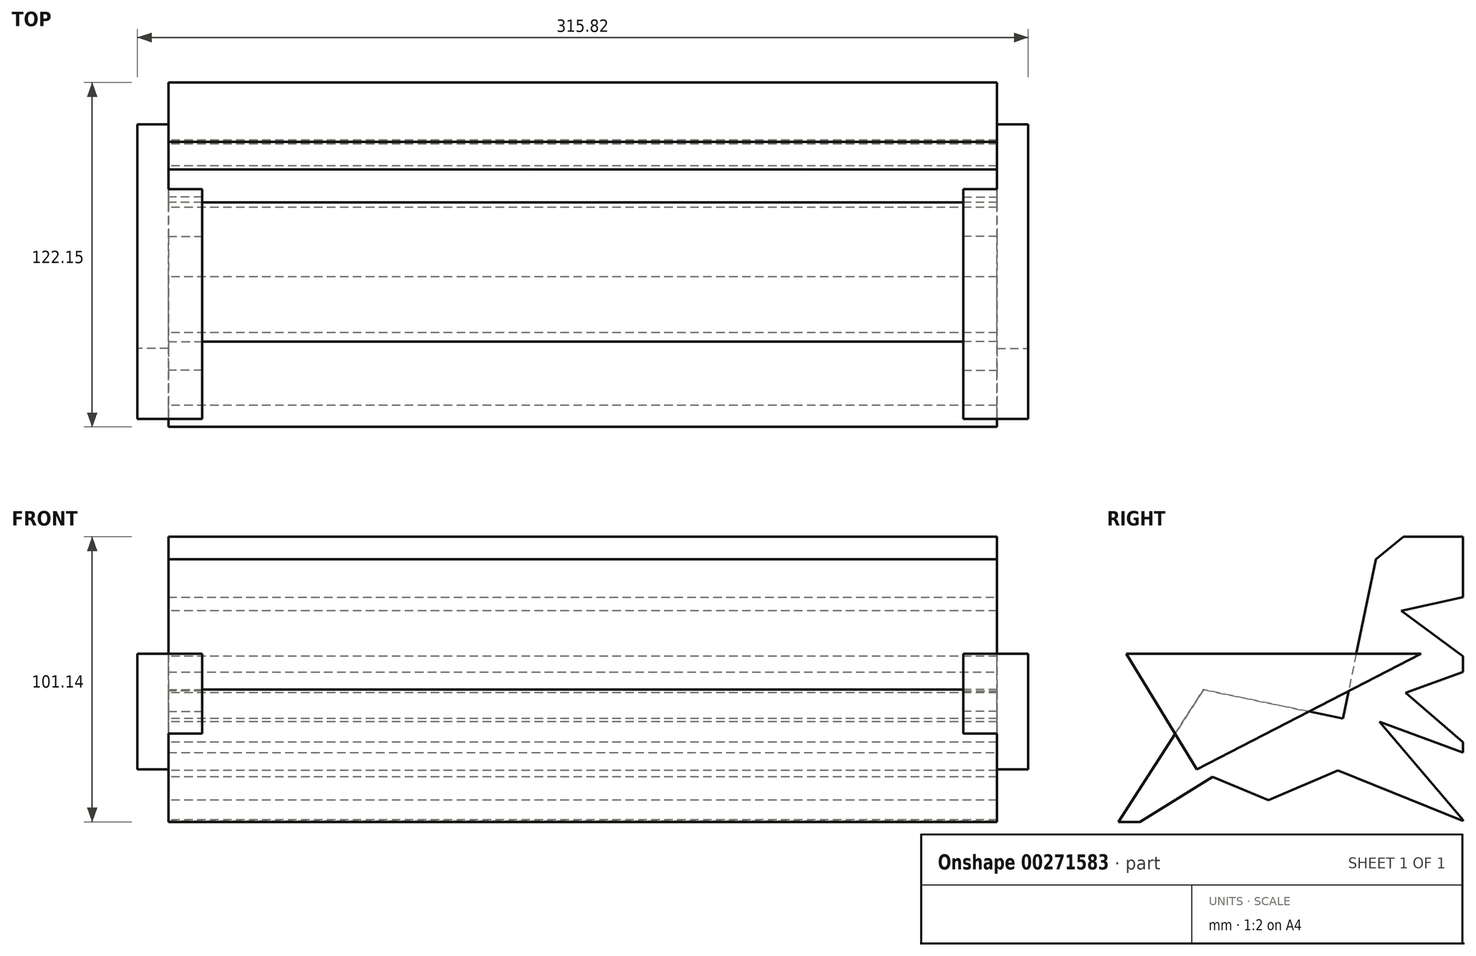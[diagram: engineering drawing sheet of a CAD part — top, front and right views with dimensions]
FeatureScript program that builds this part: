
annotation { "Feature Type Name" : "Feature", "Feature Type Description" : "" }
export const myFeature = defineFeature(function(context is Context, id is Id, definition is map)
    precondition{}
    {
        {
            var Q0;
            Q0=qCreatedBy(makeId("Front.planeOp"),FACE);
            var sketch = newSketch(context, id + "F0", { "sketchPlane" : qUnion([Q0])});
            skLineSegment(sketch, "E0.bottom", {"start": v(-146.91, -50.57) * mm, "end": v(146.91, -50.57) * mm});
            skLineSegment(sketch, "E0.top", {"start": v(-146.91, 50.57) * mm, "end": v(146.91, 50.57) * mm});
            skLineSegment(sketch, "E0.left", {"start": v(-146.91, -50.57) * mm, "end": v(-146.91, 50.57) * mm});
            skLineSegment(sketch, "E0.right", {"start": v(146.91, -50.57) * mm, "end": v(146.91, 50.57) * mm});
            skPoint(sketch, "E0.middle", {"position": v(0, 0) * mm});
            skSolve(sketch);
        }
        {
            var Q0;
            Q0=makeQuery(id+"F0.imprint","IMPRINT",FACE,{"disambiguationData":[TD([[makeQuery(id+"F0.imprint","IMPRINT",EDGE,{"derivedFrom":sQuery(id+"F0.wireOp",EDGE,"E0.bottom")}),1.0]])]});
            extrude(context, id + "F1", {"entities" : qUnion([Q0]), "endBound" : BoundingType.SYMMETRIC, "depth" : 123 * mm});
        }
        {
            var Q0;
            Q0=makeQuery(id+"F1.opExtrude","SWEPT_FACE",FACE,{"disambiguationData":[OSD([sQuery(id+"F0.wireOp",EDGE,"E0.right")])]});
            var sketch = newSketch(context, id + "F2", { "sketchPlane" : qUnion([Q0])});
            skSolve(sketch);
        }
        {
            var Q0;
            {var subQ0=sQuery(id+"F0.wireOp",EDGE,"E0.right");Q0=makeQuery(id+"F2.imprint","IMPRINT",FACE,{"disambiguationData":[TD([[makeQuery(id+"F2.imprint","IMPRINT",EDGE,{"derivedFrom":makeQuery(id+"F1.opExtrude","CAP_EDGE",EDGE,{"disambiguationData":[OSD([subQ0])],"isStart":true})}),1.0]])]});}
            var sketch = newSketch(context, id + "F3", { "sketchPlane" : qUnion([Q0])});
            skLineSegment(sketch, "E1", {"start": v(34.34, 60.4) * mm, "end": v(18.95, -13.91) * mm});
            skLineSegment(sketch, "E2", {"start": v(18.95, -13.91) * mm, "end": v(-30.46, -3.68) * mm});
            skLineSegment(sketch, "E3", {"start": v(-30.46, -3.68) * mm, "end": v(-66.02, -58.91) * mm});
            skLineSegment(sketch, "E4", {"start": v(-66.02, -58.91) * mm, "end": v(-66.02, 65.43) * mm});
            skLineSegment(sketch, "E5", {"start": v(-66.02, 65.43) * mm, "end": v(34.34, 60.4) * mm});
            skSolve(sketch);
        }
        {
            var Q0;
            Q0 = qSketchRegion(id + "F3", true);
            extrude(context, id + "F4", {"entities" : qUnion([Q0]), "operationType" : NewBodyOperationType.REMOVE, "oppositeDirection" : true, "depth" : 334 * mm});
        }
        {
            var Q0;
            {var subQ0=sQuery(id+"F0.wireOp",EDGE,"E0.right");Q0=makeQuery(id+"F2.imprint","IMPRINT",FACE,{"disambiguationData":[TD([[makeQuery(id+"F2.imprint","IMPRINT",EDGE,{"derivedFrom":makeQuery(id+"F1.opExtrude","CAP_EDGE",EDGE,{"disambiguationData":[OSD([subQ0])],"isStart":true})}),1.0]])]});}
            var sketch = newSketch(context, id + "F5", { "sketchPlane" : qUnion([Q0])});
            skLineSegment(sketch, "E6", {"start": v(-32.8, -31.9) * mm, "end": v(-57.89, 9.1) * mm});
            skLineSegment(sketch, "E7", {"start": v(-57.89, 9.1) * mm, "end": v(46.73, 9.1) * mm});
            skLineSegment(sketch, "E8", {"start": v(46.73, 9.1) * mm, "end": v(-32.8, -31.9) * mm});
            skSolve(sketch);
        }
        {
            var Q0;
            Q0=makeQuery(id+"F5.imprint","IMPRINT",FACE,{"disambiguationData":[TD([[makeQuery(id+"F5.imprint","IMPRINT",EDGE,{"derivedFrom":sQuery(id+"F5.wireOp",EDGE,"E6")}),-1.0]])]});
            extrude(context, id + "F6", {"entities" : qUnion([Q0]), "oppositeDirection" : true, "depth" : 12 * mm, "hasSecondDirection" : true, "secondDirectionOppositeDirection" : false, "secondDirectionDepth" : 11 * mm, "offsetDistance" : 25 * mm});
        }
        {
            var Q0;
            Q0=makeQuery(id+"F1.opExtrude","SWEPT_BODY",BODY,{"disambiguationData":[OSD([sQuery(id+"F0.wireOp",EDGE,"E0.bottom"),sQuery(id+"F0.wireOp",EDGE,"E0.top"),sQuery(id+"F0.wireOp",EDGE,"E0.left"),sQuery(id+"F0.wireOp",EDGE,"E0.right")])]});
            var Q1;
            Q1=qCreatedBy(makeId("Right.planeOp"),FACE);
            mirror(context, id + "F7", {"operationType" : NewBodyOperationType.ADD, "entities" : qUnion([Q0]), "mirrorPlane" : qUnion([Q1])});
        }
        {
            var Q0;
            Q0=makeQuery(id+"F4.boolean.opBoolean","INTERSECT",EDGE,{"derivedFrom":[makeQuery(id+"F1.opExtrude","SWEPT_FACE",FACE,{"disambiguationData":[OSD([sQuery(id+"F0.wireOp",EDGE,"E0.top")])]}),makeQuery(id+"F4.opExtrude","SWEPT_FACE",FACE,{"disambiguationData":[OSD([sQuery(id+"F3.wireOp",EDGE,"E1")])]})]});
            chamfer(context, id + "F8", {"entities" : qUnion([Q0]), "width" : 10 * mm, "tangentPropagation" : true});
        }
        {
            var Q0;
            Q0=qCreatedBy(makeId("Right.planeOp"),FACE);
            var sketch = newSketch(context, id + "F9", { "sketchPlane" : qUnion([Q0])});
            skLineSegment(sketch, "E9", {"start": v(69.28, 30.79) * mm, "end": v(39.67, 24.28) * mm});
            skLineSegment(sketch, "E10", {"start": v(39.67, 24.28) * mm, "end": v(66.61, 4.44) * mm});
            skLineSegment(sketch, "E11", {"start": v(66.61, 4.44) * mm, "end": v(41.15, -4.74) * mm});
            skLineSegment(sketch, "E12", {"start": v(41.15, -4.74) * mm, "end": v(68.98, -28.72) * mm});
            skLineSegment(sketch, "E13", {"start": v(68.98, -28.72) * mm, "end": v(31.97, -15.1) * mm});
            skLineSegment(sketch, "E14", {"start": v(31.97, -15.1) * mm, "end": v(61.87, -50.33) * mm});
            skLineSegment(sketch, "E15", {"start": v(61.87, -50.33) * mm, "end": v(17.17, -32.27) * mm});
            skLineSegment(sketch, "E16", {"start": v(17.17, -32.27) * mm, "end": v(-7.4, -42.93) * mm});
            skLineSegment(sketch, "E17", {"start": v(-7.4, -42.93) * mm, "end": v(-27.24, -34.64) * mm});
            skLineSegment(sketch, "E18", {"start": v(-27.24, -34.64) * mm, "end": v(-55.07, -51.8) * mm});
            skLineSegment(sketch, "E19", {"start": v(-55.07, -51.8) * mm, "end": v(-46.79, -65.23) * mm});
            skLineSegment(sketch, "E20", {"start": v(-46.79, -65.23) * mm, "end": v(78.75, -65.23) * mm});
            skLineSegment(sketch, "E21", {"start": v(78.75, -65.23) * mm, "end": v(69.28, 30.79) * mm});
            skSolve(sketch);
        }
        {
            var Q0;
            Q0=makeQuery(id+"F9.imprint","IMPRINT",FACE,{"disambiguationData":[TD([[makeQuery(id+"F9.imprint","IMPRINT",EDGE,{"derivedFrom":sQuery(id+"F9.wireOp",EDGE,"E9")}),1.0]])]});
            extrude(context, id + "F10", {"entities" : qUnion([Q0]), "operationType" : NewBodyOperationType.REMOVE, "endBound" : BoundingType.SYMMETRIC, "oppositeDirection" : true, "depth" : 370 * mm});
        }
        {
            var Q0;
            Q0=makeQuery(id+"F6.opExtrude","SWEPT_BODY",BODY,{"disambiguationData":[OSD([sQuery(id+"F5.wireOp",EDGE,"E6"),sQuery(id+"F5.wireOp",EDGE,"E7"),sQuery(id+"F5.wireOp",EDGE,"E8")])]});
            var Q1;
            Q1=qCreatedBy(makeId("Right.planeOp"),FACE);
            mirror(context, id + "F11", {"entities" : qUnion([Q0]), "mirrorPlane" : qUnion([Q1])});
        }
    });
